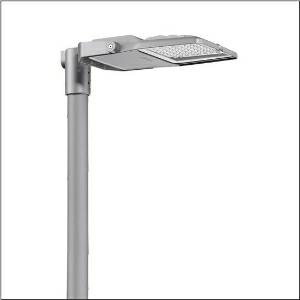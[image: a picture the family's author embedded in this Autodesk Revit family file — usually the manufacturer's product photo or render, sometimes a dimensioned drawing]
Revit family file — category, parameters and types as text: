
# Revit family: floodlight_fl_21_mini___pl43_5xa7776d2a3a_6ee6
name_source: partatom
category: Lighting Fixtures
units: mm (PartAtom-declared; Revit-internal decimal feet)

## family parameters
Cut with Voids When Loaded = No
Host = Face
Light Source = No
Part Type = Normal
Room Calculation Point = No
Round Connector Dimension = Use Diameter
Shared = No

## types (1)
- --- (1 x LED, 18300 lm, 142.9 W, 3000K)
    Apparent Load = 143 VA
    CIE Flux Codes = 27 78 99 100 100
    Color Rendering = 70
    Color Temperature = 3000K
    Default Elevation = 1800 mm
    Description = Floodlight FL 21 mini, floodlight, primary light control with lens, of PMMA, primary optical cover: protective disc, of toughened safety glass, transparent, light distribution: PL43, light emission: direct distribution, installation type: surface-mounted, LED, High Power LED, rated luminous flux: 18.300lm, luminous efficacy: 128lm/W, light colour: 730, colour temperature: 3000K, control gear: Smart Interface (Zhaga), control: flexible luminous flux parameterisation, time-dependent luminous flux control, constant luminous flux control, overheat protection, pre-setting: logarithmic dimming characteristic, with terminal, 6-pole, mains connection: 220..240V, AC, 50/60Hz, start of lifetime: 143W, end of service life: 151W, reduction: 63W, luminaire housing, of diecast aluminium, powder-coated, SITECO metallic grey (DB 702S), corrosivity category C5 mid according to DIN EN ISO 12944, suitable for swimming pools, chlorine-resistant, sealing non-destructively replaceable, please order mast flange separately, mast bracket, of steel, galvanised, powder-coated, SITECO metallic grey (DB 702S), Smart Interface below and above, protection rating (complete): IP66, insulation class (complete): insulation class II (safety insulation), certification: CE, ENEC, VDE, protection symbol: D, impact resistance: IK08, permissible operating ambient temperature: -40..+40°C, permissible operating ambient temperature for outdoor applications: -40..+50°C, standard: DIN EN 12944, LABS conformity tested according to VDMA 24364:2018-05, packaging unit: 1 piece

Light Distribution: PL43
    Height = 70 mm
    Lamp = 1 x LED
    Lamp Light Flux = 18300 lm
    Lamp Power = 142.9 W
    Lamp count = 1
    Length = 485 mm
    Luminous efficacy = 128 lm/W
    Manufacturer = Siteco
    ModVariant = No
    Model = 5XA7776D2A3A
    Number of Poles = 1
    OnlyDefault = Yes
    Power Factor = 1
    Product Name = Floodlight FL 21 mini | PL43
    Product group = floodlight | pylon annexe
    ProductGroupID = 6201
    Protection Class = Protection class II
    Protection Degree = IP 66
    RLX_Detail_Level = 1
    RLX_Emergency_Light_Flux = 0 lm
    RLX_Emergency_Type = 0
    RLX_Emergency_Type_DB = No
    RlxData = <blob elided: 101237 chars, md5=3efdcbd6>
    Socket = socket
    Standby Power = 0 W
    System Light Flux = 18300 lm
    System Power = 143 W
    Type Comments = factory setting: luminous flux: 100 % | dim-lin: 254 | 730 mA
    Type Image = l_1007125.jpg
    URL = http://relux.com
    VarID = @adj_160405
    Voltage = 0 V
    Weight = 0.00 kg
    Width = 337 mm

## geometry (parser evidence)
native form markers: Blend x4, Sweep x11
no freeform markers — native parametric forms only
